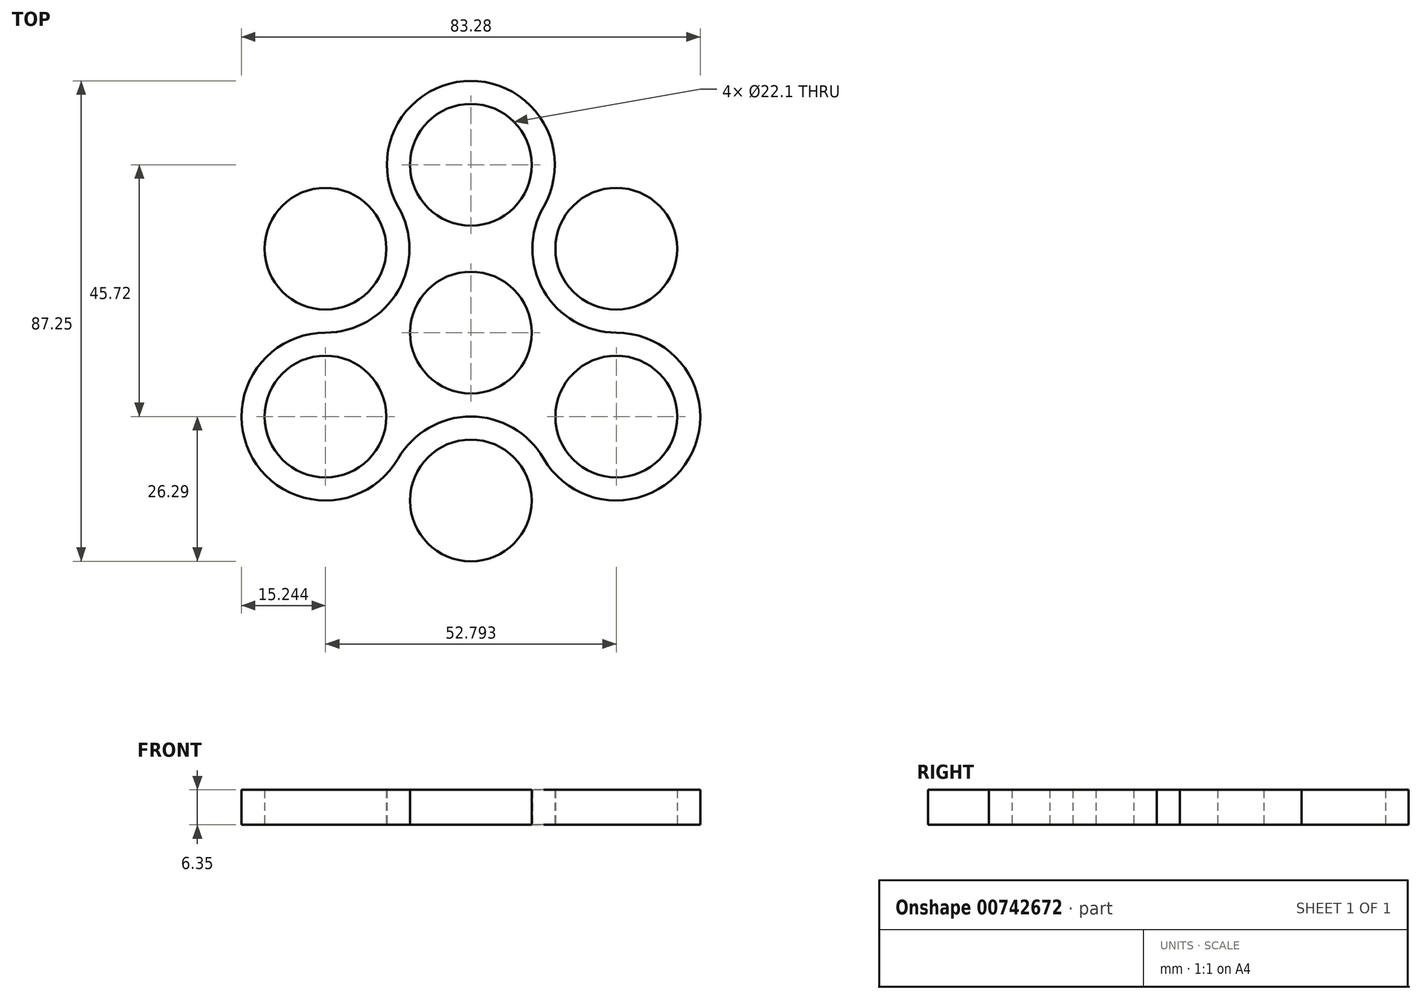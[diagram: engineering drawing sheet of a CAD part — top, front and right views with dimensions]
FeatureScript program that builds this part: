
annotation { "Feature Type Name" : "Feature", "Feature Type Description" : "" }
export const myFeature = defineFeature(function(context is Context, id is Id, definition is map)
    precondition{}
    {
        {
            var Q0;
            Q0=qCreatedBy(makeId("Top.planeOp"),FACE);
            var sketch = newSketch(context, id + "F0", { "sketchPlane" : qUnion([Q0])});
            skCircle(sketch, "E0", {"center": v(0, 0) * mm, "radius": 11.05 * mm});
            skCircle(sketch, "E1", {"center": v(0, 0) * mm, "radius": 13.97 * mm});
            skLineSegment(sketch, "E2", {"start": v(0, 0) * mm, "end": v(0, 30.48) * mm});
            skCircle(sketch, "E3", {"center": v(0, 30.48) * mm, "radius": 11.05 * mm});
            skCircle(sketch, "E4", {"center": v(0, 30.48) * mm, "radius": 15.24 * mm});
            skCircle(sketch, "E5.1.0", {"center": v(-26.4, -15.24) * mm, "radius": 15.24 * mm});
            skCircle(sketch, "E5.1.1", {"center": v(-26.4, -15.24) * mm, "radius": 11.05 * mm});
            skCircle(sketch, "E5.2.0", {"center": v(26.4, -15.24) * mm, "radius": 15.24 * mm});
            skCircle(sketch, "E5.2.1", {"center": v(26.4, -15.24) * mm, "radius": 11.05 * mm});
            skCircle(sketch, "E6.MirrorC", {"center": v(26.4, 15.24) * mm, "radius": 15.24 * mm});
            skCircle(sketch, "E7.MirrorC", {"center": v(26.4, 15.24) * mm, "radius": 11.05 * mm});
            skCircle(sketch, "E8.MirrorC", {"center": v(-26.4, 15.24) * mm, "radius": 11.05 * mm});
            skCircle(sketch, "E9.MirrorC", {"center": v(-26.4, 15.24) * mm, "radius": 15.24 * mm});
            skCircle(sketch, "E10.MirrorC", {"center": v(0, -30.48) * mm, "radius": 11.05 * mm});
            skCircle(sketch, "E11.MirrorC", {"center": v(0, -30.48) * mm, "radius": 15.24 * mm});
            skSolve(sketch);
        }
        {
            var Q0;
            Q0=makeQuery(id+"F0.imprint","IMPRINT",FACE,{"disambiguationData":[TD([[makeQuery(id+"F0.imprint","IMPRINT",EDGE,{"derivedFrom":sQuery(id+"F0.wireOp",EDGE,"E1")}),-1.0]])]});
            var Q1;
            Q1=makeQuery(id+"F0.imprint","IMPRINT",FACE,{"disambiguationData":[TD([[makeQuery(id+"F0.imprint","IMPRINT",EDGE,{"derivedFrom":sQuery(id+"F0.wireOp",EDGE,"E7.MirrorC")}),1.0]])]});
            var Q2;
            Q2=makeQuery(id+"F0.imprint","IMPRINT",FACE,{"disambiguationData":[TD([[makeQuery(id+"F0.imprint","IMPRINT",EDGE,{"derivedFrom":sQuery(id+"F0.wireOp",EDGE,"E0")}),-1.0]])]});
            var Q3;
            Q3=makeQuery(id+"F0.imprint","IMPRINT",FACE,{"disambiguationData":[TD([[makeQuery(id+"F0.imprint","IMPRINT",EDGE,{"derivedFrom":sQuery(id+"F0.wireOp",EDGE,"E3")}),-1.0]])]});
            var Q4;
            Q4=makeQuery(id+"F0.imprint","IMPRINT",FACE,{"disambiguationData":[TD([[makeQuery(id+"F0.imprint","IMPRINT",EDGE,{"derivedFrom":sQuery(id+"F0.wireOp",EDGE,"E8.MirrorC")}),1.0]])]});
            var Q5;
            Q5=makeQuery(id+"F0.imprint","IMPRINT",FACE,{"disambiguationData":[TD([[makeQuery(id+"F0.imprint","IMPRINT",EDGE,{"derivedFrom":sQuery(id+"F0.wireOp",EDGE,"E5.1.1")}),-1.0]])]});
            var Q6;
            Q6=makeQuery(id+"F0.imprint","IMPRINT",FACE,{"disambiguationData":[TD([[makeQuery(id+"F0.imprint","IMPRINT",EDGE,{"derivedFrom":sQuery(id+"F0.wireOp",EDGE,"E10.MirrorC")}),1.0]])]});
            var Q7;
            Q7=makeQuery(id+"F0.imprint","IMPRINT",FACE,{"disambiguationData":[TD([[makeQuery(id+"F0.imprint","IMPRINT",EDGE,{"derivedFrom":sQuery(id+"F0.wireOp",EDGE,"E5.2.1")}),-1.0]])]});
            extrude(context, id + "F1", {"entities" : qUnion([Q0, Q1, Q2, Q3, Q4, Q5, Q6, Q7]), "depth" : 6.35 * mm, "offsetDistance" : 25.4 * mm});
        }
    });
